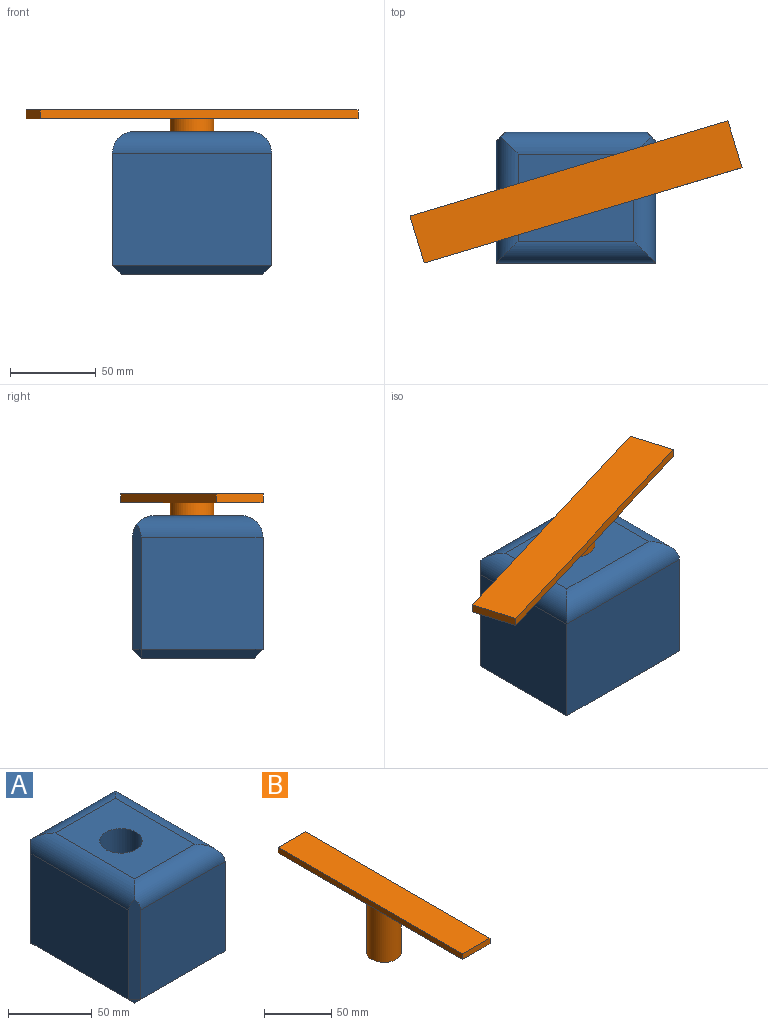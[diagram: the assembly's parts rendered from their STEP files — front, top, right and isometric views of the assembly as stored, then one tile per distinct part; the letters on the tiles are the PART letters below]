
ASSEMBLY  parts=2 mates=1
PART A: 19 faces, bbox 76.2x92.8x83.1 mm
  f0: plane 71.12x65.35mm, normal (0,1,0), area 4648mm2, adj f3,f6,f13,f18
  f1: plane 82.64x65.35mm, normal (-1,0,0), area 5400.6mm2, adj f8,f11,f13,f14
  f2: plane 71.12x65.35mm, normal (0,-1,0), area 4648mm2, adj f3,f9,f11,f15
  f3: plane 92.8x65.35mm, normal (1,0,0), area 6064.6mm2, adj f0,f2,f7,f17
  f4: plane 67.4x50.8mm, normal (0,0,1), area 2917mm2, adj f6,f7,f8,f9,f10
  f5: plane 82.64x66.04mm, normal (0,0,-1), area 4950.6mm2, adj f10,f14,f15,f17,f18
  f6: cylinder r=12.7mm len=73.66mm, axis (1,0,0), area 1308.5mm2, adj f0,f4,f7,f8,f13
  f7: cylinder r=12.7mm len=92.8mm, axis (0,-1,0), area 1667.1mm2, adj f3,f4,f6,f9
  f8: cylinder r=12.7mm len=87.72mm, axis (0,1,0), area 1612.1mm2, adj f1,f4,f6,f9,f11,f13
  f9: cylinder r=12.7mm len=73.66mm, axis (-1,0,0), area 1308.5mm2, adj f2,f4,f7,f8,f11
  f10: cylinder r=12.7mm len=83.13mm, axis (0,0,1), area 6633.8mm2, adj f4,f5
  f11: plane 72.97x5.08mm, normal (-0.71,-0.71,0), area 506.8mm2, adj f1,f2,f8,f9,f12
  f12: plane 5.08x5.08mm, normal (-0.58,-0.58,-0.58), area 22.3mm2, adj f11,f14,f15
  f13: plane 72.97x5.08mm, normal (-0.71,0.71,0), area 506.8mm2, adj f0,f1,f6,f8,f16
  f14: plane 82.64x5.08mm, normal (-0.71,0,-0.71), area 593.7mm2, adj f1,f5,f12,f16
  f15: plane 71.12x5.08mm, normal (0,-0.71,-0.71), area 492.7mm2, adj f2,f5,f12,f17
  f16: plane 5.08x5.08mm, normal (-0.58,0.58,-0.58), area 22.3mm2, adj f13,f14,f18
  f17: plane 92.8x5.08mm, normal (0.71,0,-0.71), area 630.2mm2, adj f3,f5,f15,f18
  f18: plane 71.12x5.08mm, normal (0,0.71,-0.71), area 492.7mm2, adj f0,f5,f16,f17
PART B: 8 faces, bbox 28.6x193.5x54.2 mm
  f0: cylinder r=12.7mm len=49.14mm, axis (0,0,-1), area 3920.9mm2, adj f1,f7
  f1: plane 25.4x25.4mm, normal (0,0,-1), area 506.7mm2, adj f0
  f2: plane 28.6x5.08mm, normal (0,-1,0), area 145.3mm2, adj f3,f5,f6,f7
  f3: plane 193.55x5.08mm, normal (1,0,0), area 983.2mm2, adj f2,f4,f6,f7
  f4: plane 28.6x5.08mm, normal (0,1,0), area 145.3mm2, adj f3,f5,f6,f7
  f5: plane 193.55x5.08mm, normal (-1,0,0), area 983.2mm2, adj f2,f4,f6,f7
  f6: plane 193.55x28.6mm, normal (0,0,1), area 5535.9mm2, adj f2,f3,f4,f5
  f7: plane 193.55x28.6mm, normal (0,0,-1), area 5029.2mm2, adj f0,f2,f3,f4,f5
PLACE A rot(axis=(0,0,-1),90deg) t=(35.75,3.34,0)mm
PLACE B rot(axis=(0,0,1),106.7deg) t=(41.32,3.34,41.57)mm
MATE revolute B.f0 <-> A.f10  axis (0,0,-1) through (41.32,3.34,41.57)mm
